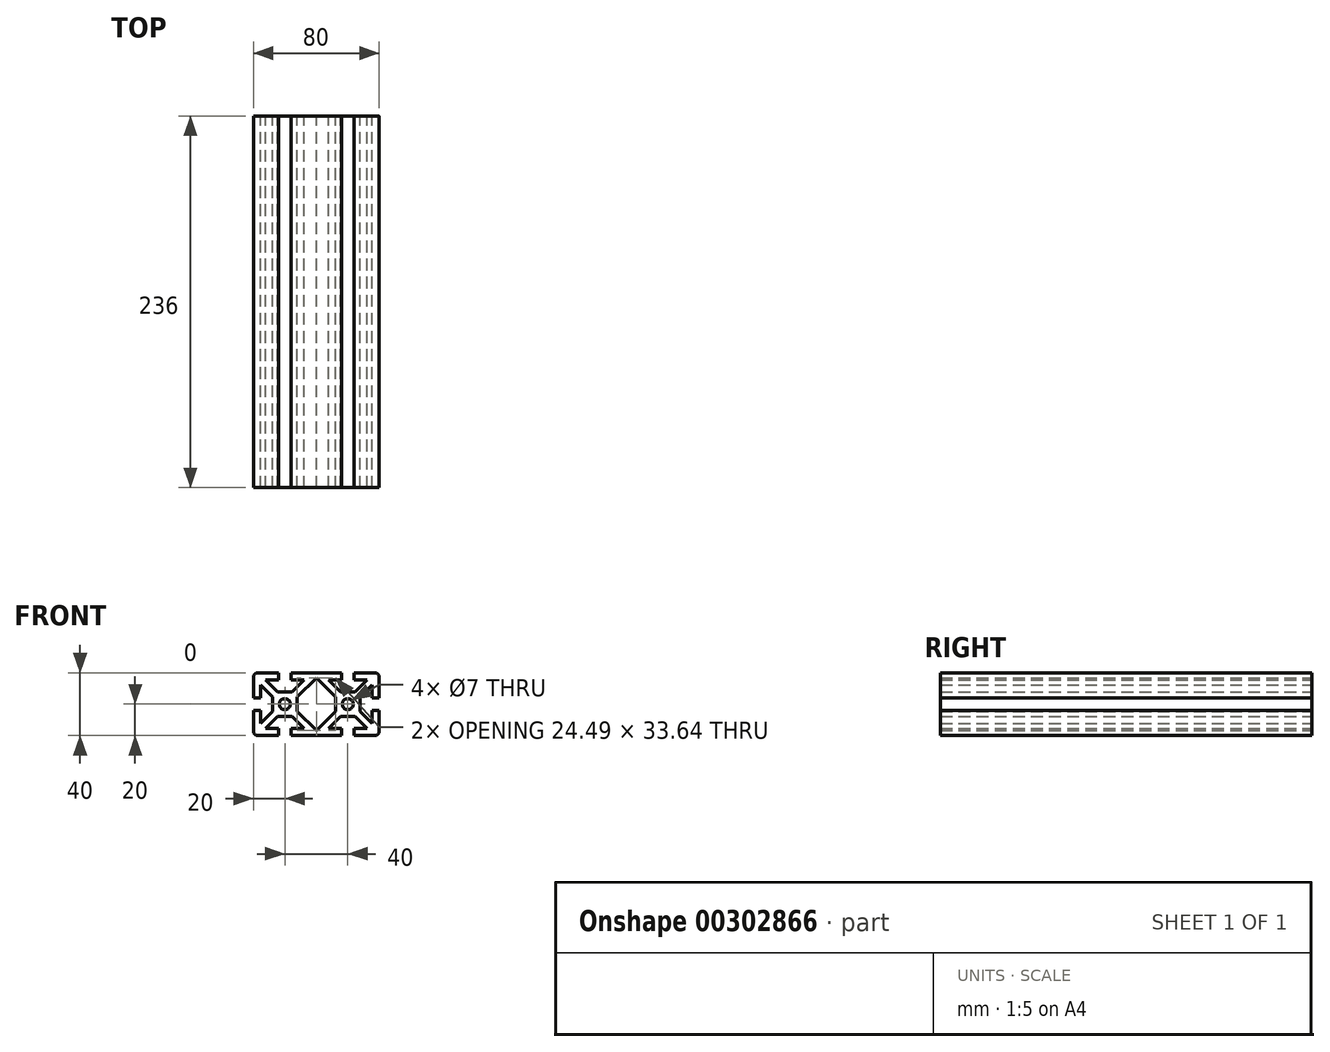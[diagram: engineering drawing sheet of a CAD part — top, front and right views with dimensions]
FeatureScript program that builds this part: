
annotation { "Feature Type Name" : "Feature", "Feature Type Description" : "" }
export const myFeature = defineFeature(function(context is Context, id is Id, definition is map)
    precondition{}
    {
        {
            var Q0;
            Q0=qCreatedBy(makeId("Front.planeOp"),FACE);
            var sketch = newSketch(context, id + "F0", { "sketchPlane" : qUnion([Q0])});
            skLineSegment(sketch, "E0", {"start": v(-106.54, 61.62) * mm, "end": v(-94.3, 49.38) * mm});
            skLineSegment(sketch, "E1", {"start": v(-94.3, 49.38) * mm, "end": v(-82.06, 61.62) * mm});
            skLineSegment(sketch, "E2", {"start": v(-82.06, 61.62) * mm, "end": v(-82.06, 70.78) * mm});
            skLineSegment(sketch, "E3", {"start": v(-82.06, 70.78) * mm, "end": v(-94.3, 83.02) * mm});
            skLineSegment(sketch, "E4", {"start": v(-94.3, 83.02) * mm, "end": v(-106.54, 70.78) * mm});
            skLineSegment(sketch, "E5", {"start": v(-106.54, 70.78) * mm, "end": v(-106.54, 61.62) * mm});
            skCircle(sketch, "E6", {"center": v(-74.3, 66.2) * mm, "radius": 3.5 * mm});
            skCircle(sketch, "E7", {"center": v(-114.3, 66.2) * mm, "radius": 3.5 * mm});
            skLineSegment(sketch, "E8", {"start": v(-129.6, 78.32) * mm, "end": v(-122.06, 70.78) * mm});
            skLineSegment(sketch, "E9", {"start": v(-122.06, 70.78) * mm, "end": v(-122.06, 61.62) * mm});
            skLineSegment(sketch, "E10", {"start": v(-122.06, 61.62) * mm, "end": v(-129.6, 54.08) * mm});
            skLineSegment(sketch, "E11", {"start": v(-129.6, 54.08) * mm, "end": v(-129.6, 62.2) * mm});
            skLineSegment(sketch, "E12", {"start": v(-129.6, 62.2) * mm, "end": v(-134.3, 62.2) * mm});
            skLineSegment(sketch, "E13", {"start": v(-134.3, 62.2) * mm, "end": v(-134.3, 49.2) * mm});
            skArc(sketch, "E14", {"start": v(-134.3, 49.2) * mm, "mid": v(-133.42, 47.08) * mm, "end": v(-131.3, 46.2) * mm});
            skLineSegment(sketch, "E15", {"start": v(-131.3, 46.2) * mm, "end": v(-118.3, 46.2) * mm});
            skLineSegment(sketch, "E16", {"start": v(-118.3, 46.2) * mm, "end": v(-118.3, 50.9) * mm});
            skLineSegment(sketch, "E17", {"start": v(-118.3, 50.9) * mm, "end": v(-126.42, 50.9) * mm});
            skLineSegment(sketch, "E18", {"start": v(-126.42, 50.9) * mm, "end": v(-118.88, 58.44) * mm});
            skLineSegment(sketch, "E19", {"start": v(-118.88, 58.44) * mm, "end": v(-109.72, 58.44) * mm});
            skLineSegment(sketch, "E20", {"start": v(-109.72, 58.44) * mm, "end": v(-102.18, 50.9) * mm});
            skLineSegment(sketch, "E21", {"start": v(-102.18, 50.9) * mm, "end": v(-110.3, 50.9) * mm});
            skLineSegment(sketch, "E22", {"start": v(-110.3, 50.9) * mm, "end": v(-110.3, 46.2) * mm});
            skLineSegment(sketch, "E23", {"start": v(-110.3, 46.2) * mm, "end": v(-78.3, 46.2) * mm});
            skLineSegment(sketch, "E24", {"start": v(-78.3, 46.2) * mm, "end": v(-78.3, 50.9) * mm});
            skLineSegment(sketch, "E25", {"start": v(-78.3, 50.9) * mm, "end": v(-86.42, 50.9) * mm});
            skLineSegment(sketch, "E26", {"start": v(-86.42, 50.9) * mm, "end": v(-78.88, 58.44) * mm});
            skLineSegment(sketch, "E27", {"start": v(-78.88, 58.44) * mm, "end": v(-69.72, 58.44) * mm});
            skLineSegment(sketch, "E28", {"start": v(-69.72, 58.44) * mm, "end": v(-62.18, 50.9) * mm});
            skLineSegment(sketch, "E29", {"start": v(-62.18, 50.9) * mm, "end": v(-70.3, 50.9) * mm});
            skLineSegment(sketch, "E30", {"start": v(-70.3, 50.9) * mm, "end": v(-70.3, 46.2) * mm});
            skLineSegment(sketch, "E31", {"start": v(-70.3, 46.2) * mm, "end": v(-57.3, 46.2) * mm});
            skArc(sketch, "E32", {"start": v(-57.3, 46.2) * mm, "mid": v(-55.18, 47.08) * mm, "end": v(-54.3, 49.2) * mm});
            skLineSegment(sketch, "E33", {"start": v(-54.3, 49.2) * mm, "end": v(-54.3, 62.2) * mm});
            skLineSegment(sketch, "E34", {"start": v(-54.3, 62.2) * mm, "end": v(-59, 62.2) * mm});
            skLineSegment(sketch, "E35", {"start": v(-59, 62.2) * mm, "end": v(-59, 54.08) * mm});
            skLineSegment(sketch, "E36", {"start": v(-59, 54.08) * mm, "end": v(-66.54, 61.62) * mm});
            skLineSegment(sketch, "E37", {"start": v(-66.54, 61.62) * mm, "end": v(-66.54, 70.78) * mm});
            skLineSegment(sketch, "E38", {"start": v(-66.54, 70.78) * mm, "end": v(-59, 78.32) * mm});
            skLineSegment(sketch, "E39", {"start": v(-59, 78.32) * mm, "end": v(-59, 70.2) * mm});
            skLineSegment(sketch, "E40", {"start": v(-59, 70.2) * mm, "end": v(-54.3, 70.2) * mm});
            skLineSegment(sketch, "E41", {"start": v(-54.3, 70.2) * mm, "end": v(-54.3, 83.2) * mm});
            skArc(sketch, "E42", {"start": v(-54.3, 83.2) * mm, "mid": v(-55.18, 85.32) * mm, "end": v(-57.3, 86.2) * mm});
            skLineSegment(sketch, "E43", {"start": v(-57.3, 86.2) * mm, "end": v(-70.3, 86.2) * mm});
            skLineSegment(sketch, "E44", {"start": v(-70.3, 86.2) * mm, "end": v(-70.3, 81.5) * mm});
            skLineSegment(sketch, "E45", {"start": v(-70.3, 81.5) * mm, "end": v(-62.18, 81.5) * mm});
            skLineSegment(sketch, "E46", {"start": v(-62.18, 81.5) * mm, "end": v(-69.72, 73.96) * mm});
            skLineSegment(sketch, "E47", {"start": v(-69.72, 73.96) * mm, "end": v(-78.88, 73.96) * mm});
            skLineSegment(sketch, "E48", {"start": v(-78.88, 73.96) * mm, "end": v(-86.42, 81.5) * mm});
            skLineSegment(sketch, "E49", {"start": v(-86.42, 81.5) * mm, "end": v(-78.3, 81.5) * mm});
            skLineSegment(sketch, "E50", {"start": v(-78.3, 81.5) * mm, "end": v(-78.3, 86.2) * mm});
            skLineSegment(sketch, "E51", {"start": v(-78.3, 86.2) * mm, "end": v(-110.3, 86.2) * mm});
            skLineSegment(sketch, "E52", {"start": v(-110.3, 86.2) * mm, "end": v(-110.3, 81.5) * mm});
            skLineSegment(sketch, "E53", {"start": v(-110.3, 81.5) * mm, "end": v(-102.18, 81.5) * mm});
            skLineSegment(sketch, "E54", {"start": v(-102.18, 81.5) * mm, "end": v(-109.72, 73.96) * mm});
            skLineSegment(sketch, "E55", {"start": v(-109.72, 73.96) * mm, "end": v(-118.88, 73.96) * mm});
            skLineSegment(sketch, "E56", {"start": v(-118.88, 73.96) * mm, "end": v(-126.42, 81.5) * mm});
            skLineSegment(sketch, "E57", {"start": v(-126.42, 81.5) * mm, "end": v(-118.3, 81.5) * mm});
            skLineSegment(sketch, "E58", {"start": v(-118.3, 81.5) * mm, "end": v(-118.3, 86.2) * mm});
            skLineSegment(sketch, "E59", {"start": v(-118.3, 86.2) * mm, "end": v(-131.3, 86.2) * mm});
            skArc(sketch, "E60", {"start": v(-131.3, 86.2) * mm, "mid": v(-133.42, 85.32) * mm, "end": v(-134.3, 83.2) * mm});
            skLineSegment(sketch, "E61", {"start": v(-134.3, 83.2) * mm, "end": v(-134.3, 70.2) * mm});
            skLineSegment(sketch, "E62", {"start": v(-134.3, 70.2) * mm, "end": v(-129.6, 70.2) * mm});
            skLineSegment(sketch, "E63", {"start": v(-129.6, 70.2) * mm, "end": v(-129.6, 78.32) * mm});
            skLineSegment(sketch, "E64", {"start": v(-131.3, 83.2) * mm, "end": v(-131.3, 85.74) * mm});
            skLineSegment(sketch, "E65", {"start": v(-131.3, 83.2) * mm, "end": v(-133.84, 83.2) * mm});
            skLineSegment(sketch, "E66", {"start": v(-131.3, 83.2) * mm, "end": v(-131.3, 80.66) * mm});
            skLineSegment(sketch, "E67", {"start": v(-131.3, 83.2) * mm, "end": v(-128.76, 83.2) * mm});
            skLineSegment(sketch, "E68", {"start": v(-57.3, 83.2) * mm, "end": v(-57.3, 85.74) * mm});
            skLineSegment(sketch, "E69", {"start": v(-57.3, 83.2) * mm, "end": v(-59.84, 83.2) * mm});
            skLineSegment(sketch, "E70", {"start": v(-57.3, 83.2) * mm, "end": v(-57.3, 80.66) * mm});
            skLineSegment(sketch, "E71", {"start": v(-57.3, 83.2) * mm, "end": v(-54.76, 83.2) * mm});
            skLineSegment(sketch, "E72", {"start": v(-57.3, 49.2) * mm, "end": v(-57.3, 51.74) * mm});
            skLineSegment(sketch, "E73", {"start": v(-57.3, 49.2) * mm, "end": v(-59.84, 49.2) * mm});
            skLineSegment(sketch, "E74", {"start": v(-57.3, 49.2) * mm, "end": v(-57.3, 46.66) * mm});
            skLineSegment(sketch, "E75", {"start": v(-57.3, 49.2) * mm, "end": v(-54.76, 49.2) * mm});
            skLineSegment(sketch, "E76", {"start": v(-131.3, 49.2) * mm, "end": v(-131.3, 51.74) * mm});
            skLineSegment(sketch, "E77", {"start": v(-131.3, 49.2) * mm, "end": v(-133.84, 49.2) * mm});
            skLineSegment(sketch, "E78", {"start": v(-131.3, 49.2) * mm, "end": v(-131.3, 46.66) * mm});
            skLineSegment(sketch, "E79", {"start": v(-131.3, 49.2) * mm, "end": v(-128.76, 49.2) * mm});
            skLineSegment(sketch, "E80", {"start": v(-114.3, 66.2) * mm, "end": v(-114.3, 68.7) * mm});
            skLineSegment(sketch, "E81", {"start": v(-114.3, 66.2) * mm, "end": v(-116.8, 66.2) * mm});
            skLineSegment(sketch, "E82", {"start": v(-114.3, 66.2) * mm, "end": v(-114.3, 63.7) * mm});
            skLineSegment(sketch, "E83", {"start": v(-114.3, 66.2) * mm, "end": v(-111.8, 66.2) * mm});
            skLineSegment(sketch, "E84", {"start": v(-114.3, 71.2) * mm, "end": v(-114.3, 72.2) * mm});
            skLineSegment(sketch, "E85", {"start": v(-119.3, 66.2) * mm, "end": v(-120.3, 66.2) * mm});
            skLineSegment(sketch, "E86", {"start": v(-114.3, 61.2) * mm, "end": v(-114.3, 60.2) * mm});
            skLineSegment(sketch, "E87", {"start": v(-109.3, 66.2) * mm, "end": v(-108.3, 66.2) * mm});
            skLineSegment(sketch, "E88", {"start": v(-74.3, 66.2) * mm, "end": v(-74.3, 68.7) * mm});
            skLineSegment(sketch, "E89", {"start": v(-74.3, 66.2) * mm, "end": v(-76.8, 66.2) * mm});
            skLineSegment(sketch, "E90", {"start": v(-74.3, 66.2) * mm, "end": v(-74.3, 63.7) * mm});
            skLineSegment(sketch, "E91", {"start": v(-74.3, 66.2) * mm, "end": v(-71.8, 66.2) * mm});
            skLineSegment(sketch, "E92", {"start": v(-74.3, 71.2) * mm, "end": v(-74.3, 72.2) * mm});
            skLineSegment(sketch, "E93", {"start": v(-79.3, 66.2) * mm, "end": v(-80.3, 66.2) * mm});
            skLineSegment(sketch, "E94", {"start": v(-74.3, 61.2) * mm, "end": v(-74.3, 60.2) * mm});
            skLineSegment(sketch, "E95", {"start": v(-69.3, 66.2) * mm, "end": v(-68.3, 66.2) * mm});
            skSolve(sketch);
        }
        {
            var Q0;
            Q0=makeQuery(id+"F0.imprint","IMPRINT",FACE,{"disambiguationData":[TD([[makeQuery(id+"F0.imprint","IMPRINT",EDGE,{"derivedFrom":sQuery(id+"F0.wireOp",EDGE,"E0")}),-1.0]])]});
            extrude(context, id + "F1", {"entities" : qUnion([Q0]), "depth" : 236 * mm});
        }
        {
            var Q0;
            Q0=makeQuery(id+"F1.opExtrude","SWEPT_BODY",BODY,{"disambiguationData":[OSD([sQuery(id+"F0.wireOp",EDGE,"E0"),sQuery(id+"F0.wireOp",EDGE,"E1"),sQuery(id+"F0.wireOp",EDGE,"E2"),sQuery(id+"F0.wireOp",EDGE,"E3"),sQuery(id+"F0.wireOp",EDGE,"E4"),sQuery(id+"F0.wireOp",EDGE,"E5"),sQuery(id+"F0.wireOp",EDGE,"E6"),sQuery(id+"F0.wireOp",EDGE,"E7"),sQuery(id+"F0.wireOp",EDGE,"E8"),sQuery(id+"F0.wireOp",EDGE,"E9"),sQuery(id+"F0.wireOp",EDGE,"E10"),sQuery(id+"F0.wireOp",EDGE,"E11"),sQuery(id+"F0.wireOp",EDGE,"E12"),sQuery(id+"F0.wireOp",EDGE,"E13"),sQuery(id+"F0.wireOp",EDGE,"E14"),sQuery(id+"F0.wireOp",EDGE,"E15"),sQuery(id+"F0.wireOp",EDGE,"E16"),sQuery(id+"F0.wireOp",EDGE,"E17"),sQuery(id+"F0.wireOp",EDGE,"E18"),sQuery(id+"F0.wireOp",EDGE,"E19"),sQuery(id+"F0.wireOp",EDGE,"E20"),sQuery(id+"F0.wireOp",EDGE,"E21"),sQuery(id+"F0.wireOp",EDGE,"E22"),sQuery(id+"F0.wireOp",EDGE,"E23"),sQuery(id+"F0.wireOp",EDGE,"E24"),sQuery(id+"F0.wireOp",EDGE,"E25"),sQuery(id+"F0.wireOp",EDGE,"E26"),sQuery(id+"F0.wireOp",EDGE,"E27"),sQuery(id+"F0.wireOp",EDGE,"E28"),sQuery(id+"F0.wireOp",EDGE,"E29"),sQuery(id+"F0.wireOp",EDGE,"E30"),sQuery(id+"F0.wireOp",EDGE,"E31"),sQuery(id+"F0.wireOp",EDGE,"E32"),sQuery(id+"F0.wireOp",EDGE,"E33"),sQuery(id+"F0.wireOp",EDGE,"E34"),sQuery(id+"F0.wireOp",EDGE,"E35"),sQuery(id+"F0.wireOp",EDGE,"E36"),sQuery(id+"F0.wireOp",EDGE,"E37"),sQuery(id+"F0.wireOp",EDGE,"E38"),sQuery(id+"F0.wireOp",EDGE,"E39"),sQuery(id+"F0.wireOp",EDGE,"E40"),sQuery(id+"F0.wireOp",EDGE,"E41"),sQuery(id+"F0.wireOp",EDGE,"E42"),sQuery(id+"F0.wireOp",EDGE,"E43"),sQuery(id+"F0.wireOp",EDGE,"E44"),sQuery(id+"F0.wireOp",EDGE,"E45"),sQuery(id+"F0.wireOp",EDGE,"E46"),sQuery(id+"F0.wireOp",EDGE,"E47"),sQuery(id+"F0.wireOp",EDGE,"E48"),sQuery(id+"F0.wireOp",EDGE,"E49"),sQuery(id+"F0.wireOp",EDGE,"E50"),sQuery(id+"F0.wireOp",EDGE,"E51"),sQuery(id+"F0.wireOp",EDGE,"E52"),sQuery(id+"F0.wireOp",EDGE,"E53"),sQuery(id+"F0.wireOp",EDGE,"E54"),sQuery(id+"F0.wireOp",EDGE,"E55"),sQuery(id+"F0.wireOp",EDGE,"E56"),sQuery(id+"F0.wireOp",EDGE,"E57"),sQuery(id+"F0.wireOp",EDGE,"E58"),sQuery(id+"F0.wireOp",EDGE,"E59"),sQuery(id+"F0.wireOp",EDGE,"E60"),sQuery(id+"F0.wireOp",EDGE,"E61"),sQuery(id+"F0.wireOp",EDGE,"E62"),sQuery(id+"F0.wireOp",EDGE,"E63")])]});
            transform(context, id + "F2", {"entities" : qUnion([Q0]), "transformType" : TransformType.TRANSLATION_3D, "dx" : 0 * mm, "dy" : 0 * mm, "dz" : 0 * mm, "makeCopy" : true});
        }
    });
